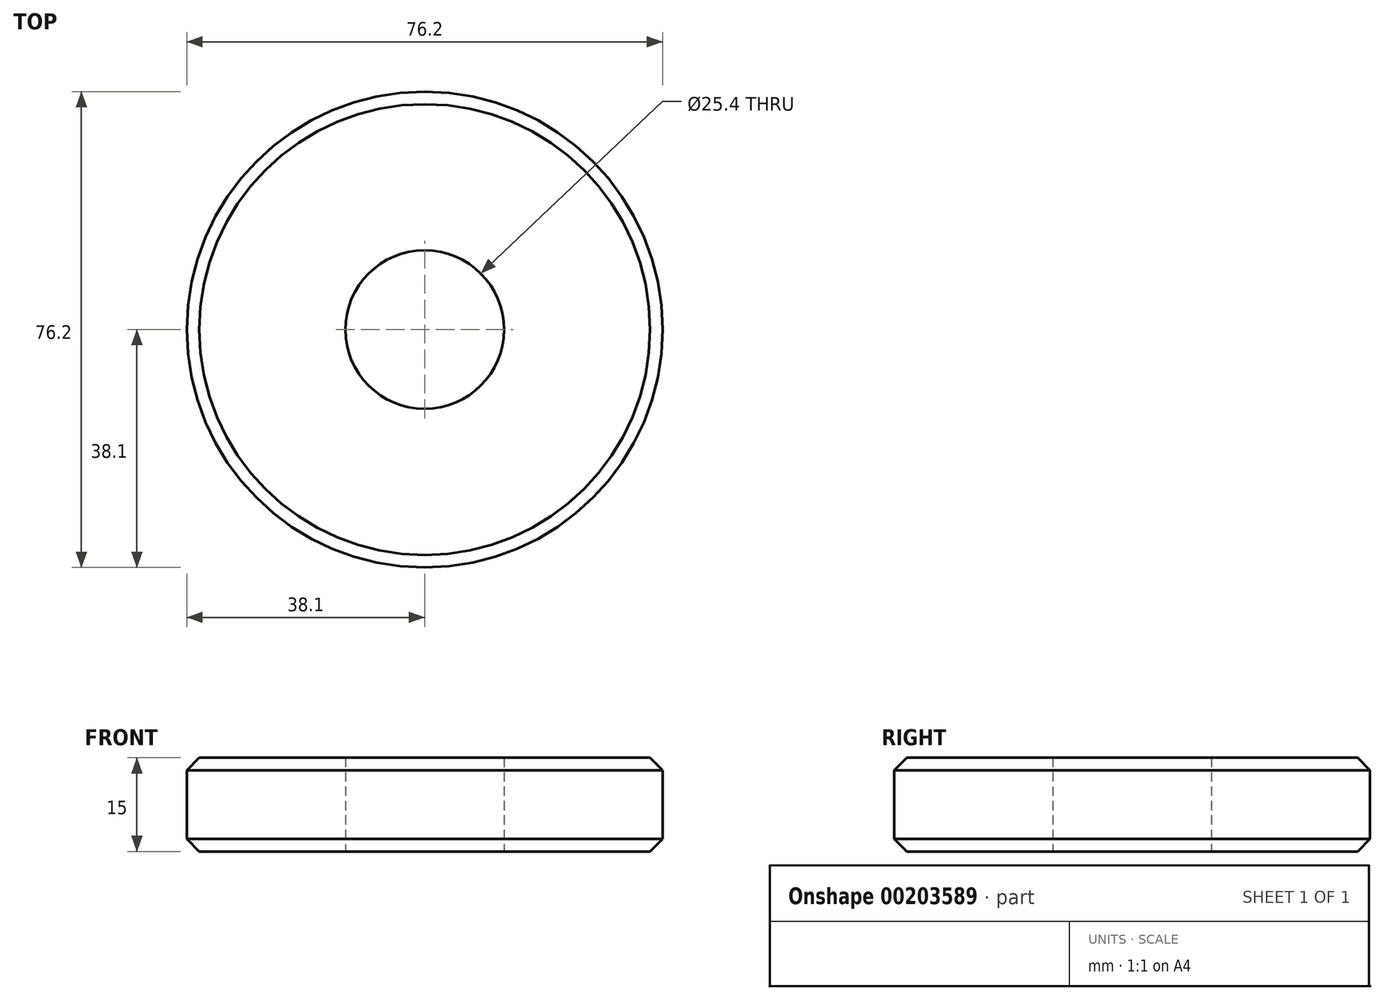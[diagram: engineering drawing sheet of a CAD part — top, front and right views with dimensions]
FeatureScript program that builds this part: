
annotation { "Feature Type Name" : "Feature", "Feature Type Description" : "" }
export const myFeature = defineFeature(function(context is Context, id is Id, definition is map)
    precondition{}
    {
        {
            var Q0;
            Q0=qCreatedBy(makeId("Top.planeOp"),FACE);
            var sketch = newSketch(context, id + "F0", { "sketchPlane" : qUnion([Q0])});
            skCircle(sketch, "E0", {"center": v(0, 0) * mm, "radius": 38.1 * mm});
            skCircle(sketch, "E1", {"center": v(0, 0) * mm, "radius": 12.7 * mm});
            skSolve(sketch);
        }
        {
            var Q0;
            Q0 = qSketchRegion(id + "F0", true);
            extrude(context, id + "F1", {"entities" : qUnion([Q0]), "depth" : 15 * mm});
        }
        {
            var Q0;
            Q0=makeQuery(id+"F1.opExtrude","CAP_EDGE",EDGE,{"disambiguationData":[OSD([sQuery(id+"F0.wireOp",EDGE,"E0")])],"isStart":false});
            var Q1;
            Q1=makeQuery(id+"F1.opExtrude","CAP_EDGE",EDGE,{"disambiguationData":[OSD([sQuery(id+"F0.wireOp",EDGE,"E0")])],"isStart":true});
            chamfer(context, id + "F2", {"entities" : qUnion([Q0, Q1]), "width" : 2 * mm, "tangentPropagation" : true});
        }
        {
            var Q0;
            Q0=qCreatedBy(makeId("Right.planeOp"),FACE);
            cPlane(context, id + "F3", {"entities" : qUnion([Q0]), "cplaneType" : CPlaneType.OFFSET, "offset" : 3 / 50.8 * mm, "width" : 150 * mm, "height" : 150 * mm});
        }
        {
            var Q0;
            Q0=qCreatedBy(id+"F3.planeOp",FACE);
            var sketch = newSketch(context, id + "F4", { "sketchPlane" : qUnion([Q0])});
            skPoint(sketch, "E2", {"position": v(0, 7.5) * mm});
            skSolve(sketch);
        }
        {
            var Q0;
            Q0=sQuery(id+"F4.wireOp",VERTEX,"E2");
            var Q1;
            Q1=makeQuery(id+"F1.opExtrude","SWEPT_BODY",BODY,{"disambiguationData":[OSD([sQuery(id+"F0.wireOp",EDGE,"E0"),sQuery(id+"F0.wireOp",EDGE,"E1")])]});
            hole(context, id + "F5", {"style" : HoleStyle.SIMPLE, "endStyle" : HoleEndStyle.BLIND, "standardTappedOrClearance" : lookupTablePath({ "standard" : "ISO", "fit" : "Normal", "size" : "M8", "type" : "Clearance" }), "standardBlindInLast" : lookupTablePath({ "fit" : "Standard", "standard" : "ISO", "size" : "M8", "type" : "Clearance" }), "holeDiameter" : 8.8 * mm, "holeDepth" : 3 / 50.8 * mm, "startFromSketch" : true, "locations" : qUnion([Q0]), "scope" : qUnion([Q1])});
        }
    });
